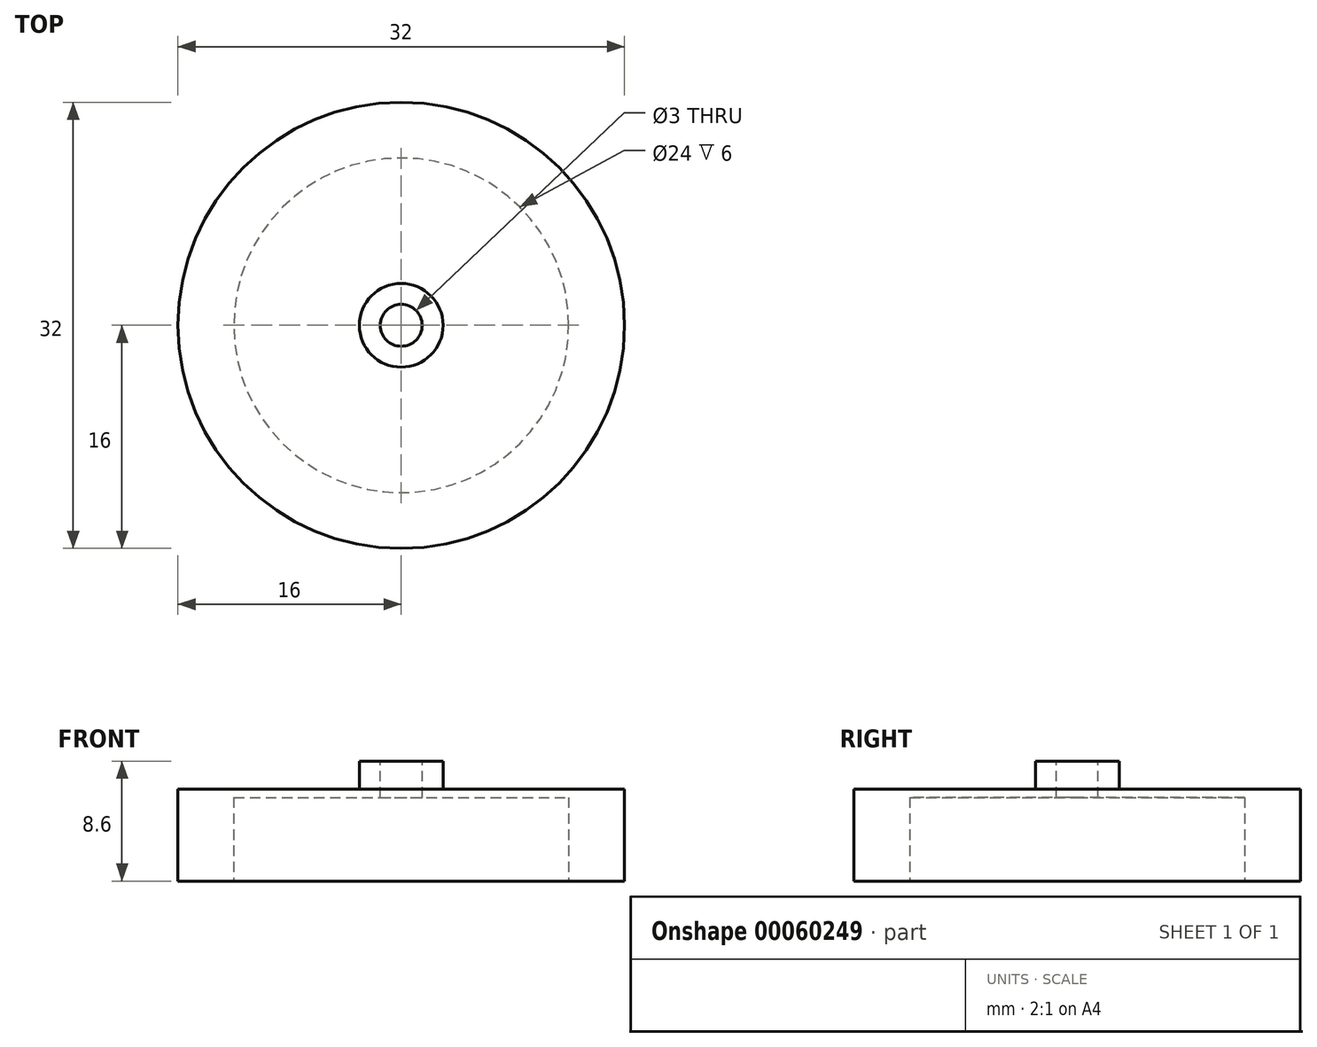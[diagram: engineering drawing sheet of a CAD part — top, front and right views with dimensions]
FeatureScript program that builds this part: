
annotation { "Feature Type Name" : "Feature", "Feature Type Description" : "" }
export const myFeature = defineFeature(function(context is Context, id is Id, definition is map)
    precondition{}
    {
        {
            var Q0;
            Q0=qCreatedBy(makeId("Top.planeOp"),FACE);
            var sketch = newSketch(context, id + "F0", { "sketchPlane" : qUnion([Q0])});
            skCircle(sketch, "E0", {"center": v(0, 0) * mm, "radius": 16 * mm});
            skSolve(sketch);
        }
        {
            var Q0;
            Q0 = qSketchRegion(id + "F0", true);
            extrude(context, id + "F1", {"entities" : qUnion([Q0]), "depth" : 6.6 * mm});
        }
        {
            var Q0;
            Q0=makeQuery(id+"F1.opExtrude","CAP_FACE",FACE,{"disambiguationData":[OSD([sQuery(id+"F0.wireOp",EDGE,"E0")])],"isStart":false});
            var sketch = newSketch(context, id + "F2", { "sketchPlane" : qUnion([Q0])});
            skCircle(sketch, "E1", {"center": v(0, 0) * mm, "radius": 3 * mm});
            skSolve(sketch);
        }
        {
            var Q0;
            Q0 = qSketchRegion(id + "F2", true);
            extrude(context, id + "F3", {"entities" : qUnion([Q0]), "operationType" : NewBodyOperationType.ADD, "depth" : 2 * mm});
        }
        {
            var Q0;
            Q0=makeQuery(id+"F3.opExtrude","CAP_FACE",FACE,{"disambiguationData":[OSD([sQuery(id+"F2.wireOp",EDGE,"E1")])],"isStart":false});
            var sketch = newSketch(context, id + "F4", { "sketchPlane" : qUnion([Q0])});
            skCircle(sketch, "E2", {"center": v(0, 0) * mm, "radius": 1.5 * mm});
            skSolve(sketch);
        }
        {
            var Q0;
            Q0 = qSketchRegion(id + "F4", true);
            extrude(context, id + "F5", {"entities" : qUnion([Q0]), "operationType" : NewBodyOperationType.REMOVE, "endBound" : BoundingType.THROUGH_ALL, "oppositeDirection" : true, "depth" : 25 * mm});
        }
        {
            var Q0;
            Q0=makeQuery(id+"F1.opExtrude","CAP_FACE",FACE,{"disambiguationData":[OSD([sQuery(id+"F0.wireOp",EDGE,"E0")])],"isStart":true});
            var sketch = newSketch(context, id + "F6", { "sketchPlane" : qUnion([Q0])});
            skCircle(sketch, "E3", {"center": v(0, 0) * mm, "radius": 12 * mm});
            skSolve(sketch);
        }
        {
            var Q0;
            Q0 = qSketchRegion(id + "F6", true);
            extrude(context, id + "F7", {"entities" : qUnion([Q0]), "operationType" : NewBodyOperationType.REMOVE, "oppositeDirection" : true, "depth" : 6 * mm});
        }
    });
